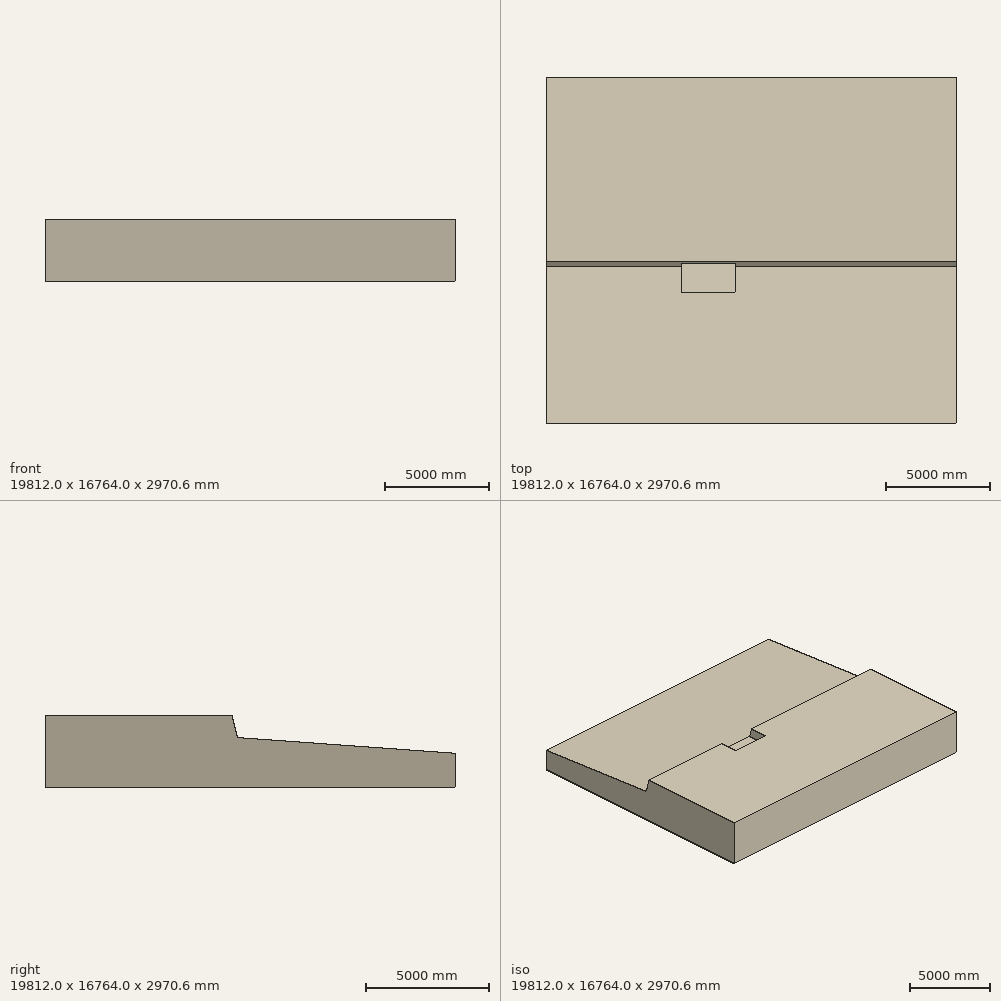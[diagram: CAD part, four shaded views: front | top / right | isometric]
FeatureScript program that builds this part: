
annotation { "Feature Type Name" : "Feature", "Feature Type Description" : "" }
export const myFeature = defineFeature(function(context is Context, id is Id, definition is map)
    precondition{}
    {
        {
            var Q0;
            Q0=qCreatedBy(makeId("Right.planeOp"),FACE);
            var sketch = newSketch(context, id + "F0", { "sketchPlane" : qUnion([Q0])});
            skLineSegment(sketch, "E0", {"start": v(-7620, -2970.56) * mm, "end": v(9144, -2970.56) * mm});
            skLineSegment(sketch, "E1", {"start": v(0, 0) * mm, "end": v(0, -1751.08) * mm, "construction": true});
            skLineSegment(sketch, "E2", {"start": v(0, 0) * mm, "end": v(227.99, -914.4) * mm});
            skLineSegment(sketch, "E3", {"start": v(-7620, -2970.56) * mm, "end": v(-7620, 0) * mm});
            skLineSegment(sketch, "E4", {"start": v(-7620, 0) * mm, "end": v(0, 0) * mm});
            skLineSegment(sketch, "E5", {"start": v(227.99, -914.4) * mm, "end": v(9144, -1558.54) * mm});
            skLineSegment(sketch, "E6", {"start": v(9144, -1558.54) * mm, "end": v(9144, -2970.56) * mm});
            skSolve(sketch);
        }
        {
            var Q0;
            Q0 = qSketchRegion(id + "F0", true);
            extrude(context, id + "F1", {"entities" : qUnion([Q0]), "depth" : 10668 * mm, "hasSecondDirection" : true, "secondDirectionOppositeDirection" : true, "secondDirectionDepth" : 9144 * mm});
        }
        {
            var Q0;
            Q0=makeQuery(id+"F1.opExtrude","SWEPT_FACE",FACE,{"disambiguationData":[OSD([sQuery(id+"F0.wireOp",EDGE,"E4")])]});
            var sketch = newSketch(context, id + "F2", { "sketchPlane" : qUnion([Q0])});
            skLineSegment(sketch, "E7.bottom", {"start": v(0, -1252.39) * mm, "end": v(-2631.47, -1252.39) * mm});
            skLineSegment(sketch, "E7.top", {"start": v(0, 1189.5) * mm, "end": v(-2631.47, 1189.5) * mm});
            skLineSegment(sketch, "E7.left", {"start": v(0, -1252.39) * mm, "end": v(0, 1189.5) * mm});
            skLineSegment(sketch, "E7.right", {"start": v(-2631.47, -1252.39) * mm, "end": v(-2631.47, 1189.5) * mm});
            skSolve(sketch);
        }
        {
            var Q0;
            Q0 = qSketchRegion(id + "F2", true);
            extrude(context, id + "F3", {"entities" : qUnion([Q0]), "operationType" : NewBodyOperationType.REMOVE, "oppositeDirection" : true, "depth" : 609.6 * mm});
        }
    });
